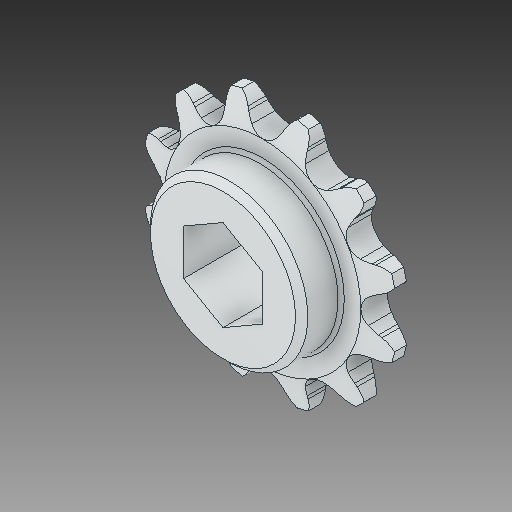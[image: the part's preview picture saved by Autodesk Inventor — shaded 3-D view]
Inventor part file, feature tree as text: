
AUTODESK INVENTOR PART (.ipt)
format: ipt  version: 2017 (Build 210142000, 142)  size: 376,320 bytes
history: native  units: in
note: dims shown in document units (in); Inventor stores cm internally (conversion verified against a paired STEP export)
features: chamfer x1
ambient origin geometry x8: Origin, YZ Plane, XZ Plane, XY Plane, X Axis, Y Axis, Z Axis, Center Point
bodies: Solid1 (feature_tree)
feature tree (1):
  chamfer  "Chamfer1"  [1 undecoded]
note: 1 required parameter value undecoded (feature->parameter linkage not recoverable at this tier; creation-order binding heuristic only, values carry confidence <= 0.55)
